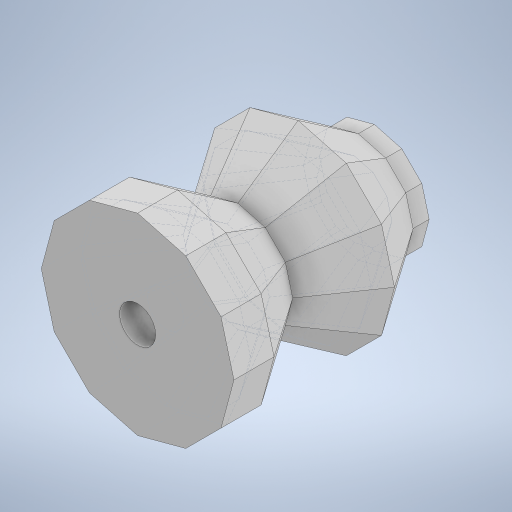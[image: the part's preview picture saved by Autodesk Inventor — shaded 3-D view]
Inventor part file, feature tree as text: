
AUTODESK INVENTOR PART (.ipt)
format: ipt  version: 2023 (Build 270158000, 158)  size: 352,768 bytes
history: native  units: in
note: dims shown in document units (in); Inventor stores cm internally (conversion verified against a paired STEP export)
features: sketch x7, extrude x5, projected_geometry x3, mirror x2, other x1, shell x1
ambient origin geometry x8: Origin, YZ Plane, XZ Plane, XY Plane, X Axis, Y Axis, Z Axis, Center Point
bodies: Body1 (feature_tree)
feature tree (19):
  other  "솔리드1"
  extrude  "돌출1"  Depth=0.9449in
  mirror  "미러1"
  mirror  "미러2"
  sketch  "스케치2"
  sketch  "스케치3"
  extrude  "돌출2"  Depth=0.2953in
  shell  "쉘1"  Thickness=0.0787in
  extrude  "돌출3"  Depth=0.0787in
  extrude  "돌출4"  Depth=0.0197in
  extrude  "돌출5"  Depth=0.1181in TaperAngle=0.0deg
  sketch  "스케치1"
  sketch  "스케치4"
  projected_geometry  "투영된 루프1"
  sketch  "스케치5"
  projected_geometry  "투영된 루프2"
  sketch  "스케치6"
  sketch  "스케치7"
  projected_geometry  "투영된 루프3"
